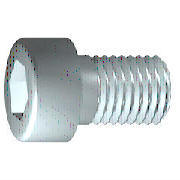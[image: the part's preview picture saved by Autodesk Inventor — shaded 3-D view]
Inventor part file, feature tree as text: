
AUTODESK INVENTOR PART (.ipt)
format: ipt  version: 2018 (Build 220112000, 112)  size: 183,296 bytes
history: native  units: mm (DEFAULTED — no unit token found)
features: sketch x2, extrude x1, plane x1, fillet x1
ambient origin geometry x7: Origin, YZ Plane, XY Plane, X Axis, Y Axis, Z Axis, Center Point
bodies: Solid1 (feature_tree), Body (feature_tree)
feature tree (5):
  extrude  "Slot"  Depth=1.5876mm
  plane  "Work Plane1"
  fillet  "Fillet2"  Radius=3.175mm
  sketch  "Sketch1"  dims[d1=19.05mm d2=1.5876mm d3=3.175mm]
  sketch  "Sketch2"  dims[d4=1.4478mm d5=60.0deg d6=3.175mm d7=3.175mm d8=2.756963mm d9=5.207mm d10=90.0deg d11=10.0mm d12=0.0mm d13=19.05mm d14=0.0mm d15=0.37846mm d16=0.37846mm d17=0.3048mm d19=0.0mm d26=38.1mm d27=45.0deg d28=0.0mm d29=0.0mm d30=0.127mm]
